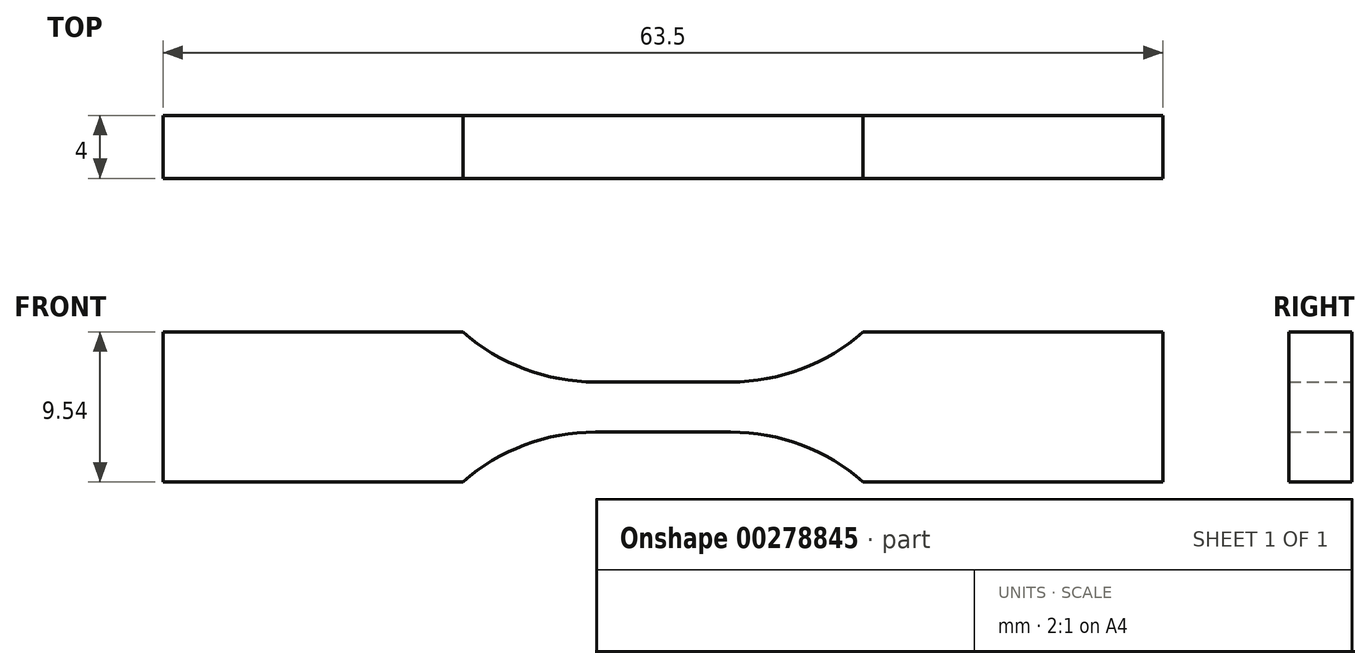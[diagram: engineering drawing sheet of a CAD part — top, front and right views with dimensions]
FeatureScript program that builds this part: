
annotation { "Feature Type Name" : "Feature", "Feature Type Description" : "" }
export const myFeature = defineFeature(function(context is Context, id is Id, definition is map)
    precondition{}
    {
        {
            var Q0;
            Q0=qCreatedBy(makeId("Front.planeOp"),FACE);
            var sketch = newSketch(context, id + "F0", { "sketchPlane" : qUnion([Q0])});
            skLineSegment(sketch, "E0", {"start": v(0, 1.6) * mm, "end": v(4.3, 1.6) * mm});
            skArc(sketch, "E1", {"start": v(4.3, 1.6) * mm, "mid": v(8.79, 2.41) * mm, "end": v(12.7, 4.77) * mm});
            skLineSegment(sketch, "E2", {"start": v(12.7, 4.77) * mm, "end": v(31.75, 4.77) * mm});
            skLineSegment(sketch, "E3.MirrorCS", {"start": v(12.7, -4.77) * mm, "end": v(31.75, -4.77) * mm});
            skLineSegment(sketch, "E4.MirrorCS", {"start": v(0, -1.6) * mm, "end": v(4.3, -1.6) * mm});
            skArc(sketch, "E5.MirrorCS", {"start": v(4.3, -1.6) * mm, "mid": v(8.79, -2.41) * mm, "end": v(12.7, -4.77) * mm});
            skLineSegment(sketch, "E6.MirrorCS", {"start": v(-12.7, 4.77) * mm, "end": v(-31.75, 4.77) * mm});
            skLineSegment(sketch, "E7.MirrorCS", {"start": v(-12.7, -4.77) * mm, "end": v(-31.75, -4.77) * mm});
            skLineSegment(sketch, "E8.MirrorCS", {"start": v(0, 1.6) * mm, "end": v(-4.3, 1.6) * mm});
            skArc(sketch, "E9.MirrorCS", {"start": v(-4.3, 1.6) * mm, "mid": v(-8.79, 2.41) * mm, "end": v(-12.7, 4.77) * mm});
            skArc(sketch, "E10.MirrorCS", {"start": v(-4.3, -1.6) * mm, "mid": v(-8.79, -2.41) * mm, "end": v(-12.7, -4.77) * mm});
            skLineSegment(sketch, "E11.MirrorCS", {"start": v(0, -1.6) * mm, "end": v(-4.3, -1.6) * mm});
            skLineSegment(sketch, "E12", {"start": v(-31.75, 4.77) * mm, "end": v(-31.75, -4.77) * mm});
            skLineSegment(sketch, "E13", {"start": v(31.75, 4.77) * mm, "end": v(31.75, -4.77) * mm});
            skSolve(sketch);
        }
        {
            var Q0;
            Q0=makeQuery(id+"F0.imprint","IMPRINT",FACE,{"disambiguationData":[TD([[makeQuery(id+"F0.imprint","IMPRINT",EDGE,{"derivedFrom":sQuery(id+"F0.wireOp",EDGE,"E1")}),-1.0]])]});
            extrude(context, id + "F1", {"entities" : qUnion([Q0]), "endBound" : BoundingType.SYMMETRIC, "depth" : 4 * mm});
        }
    });
